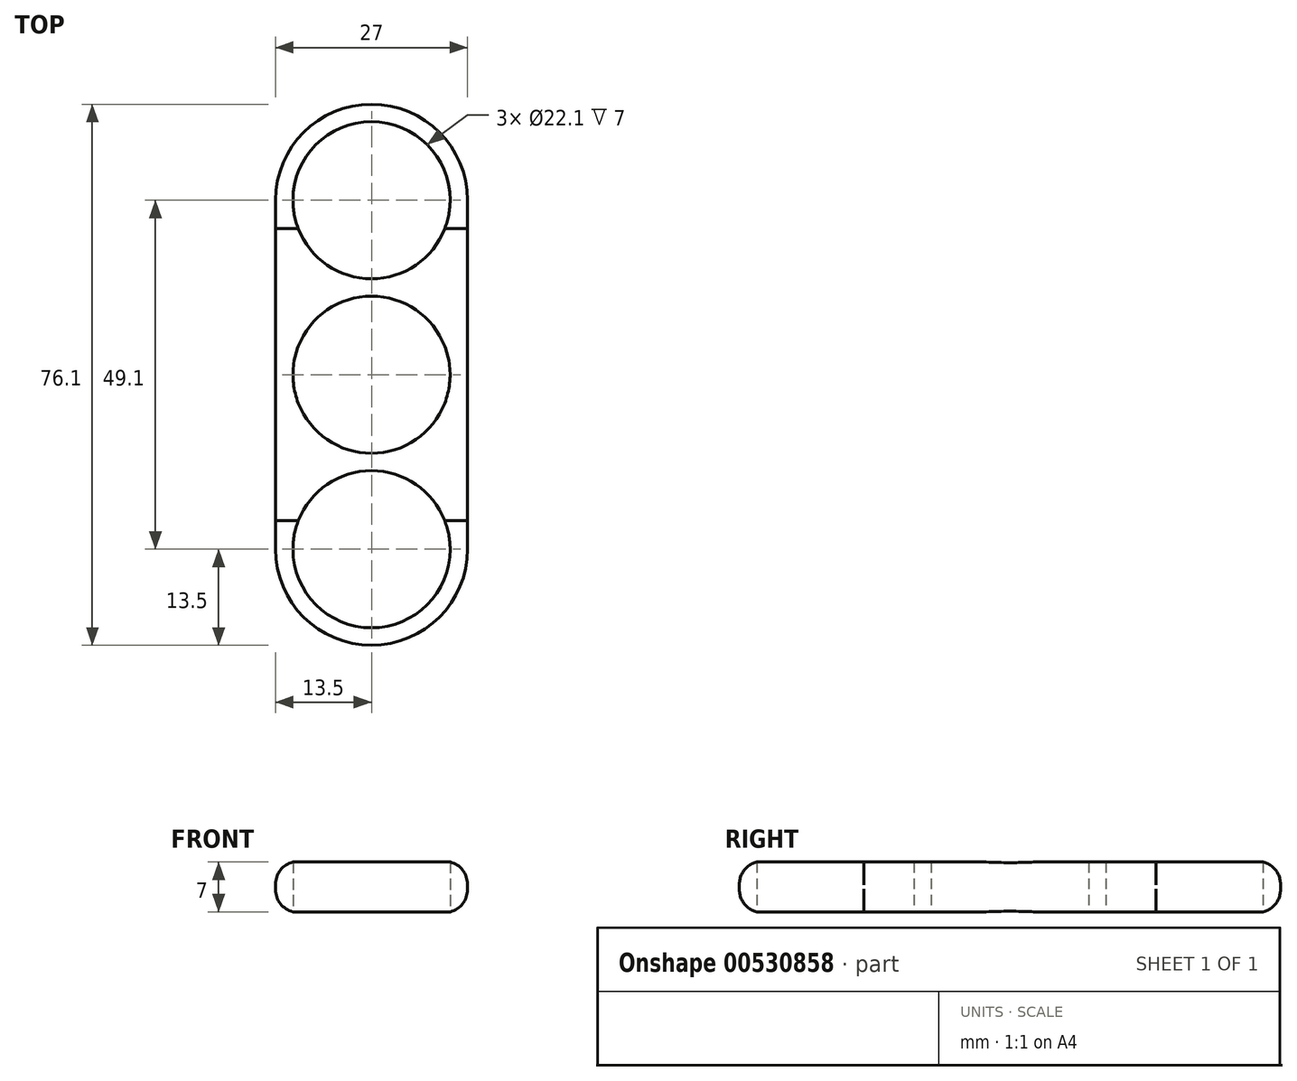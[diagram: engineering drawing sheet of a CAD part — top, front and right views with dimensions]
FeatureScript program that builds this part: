
annotation { "Feature Type Name" : "Feature", "Feature Type Description" : "" }
export const myFeature = defineFeature(function(context is Context, id is Id, definition is map)
    precondition{}
    {
        {
            var Q0;
            Q0=qCreatedBy(makeId("Top.planeOp"),FACE);
            var sketch = newSketch(context, id + "F0", { "sketchPlane" : qUnion([Q0])});
            skCircle(sketch, "E0", {"center": v(0, 0) * mm, "radius": 11.05 * mm});
            skCircle(sketch, "E1", {"center": v(0, 24.55) * mm, "radius": 11.05 * mm});
            skArc(sketch, "E2", {"start": v(13.5, 24.55) * mm, "mid": v(0, 38.05) * mm, "end": v(-13.5, 24.55) * mm});
            skCircle(sketch, "E3", {"center": v(0, -24.55) * mm, "radius": 11.05 * mm});
            skArc(sketch, "E4", {"start": v(-13.5, -24.55) * mm, "mid": v(0, -38.05) * mm, "end": v(13.5, -24.55) * mm});
            skLineSegment(sketch, "E5", {"start": v(13.5, -24.55) * mm, "end": v(13.5, 24.55) * mm});
            skLineSegment(sketch, "E6", {"start": v(-13.5, 24.55) * mm, "end": v(-13.5, -24.55) * mm});
            skSolve(sketch);
        }
        {
            var Q0;
            Q0=makeQuery(id+"F0.imprint","IMPRINT",FACE,{"disambiguationData":[TD([[makeQuery(id+"F0.imprint","IMPRINT",EDGE,{"derivedFrom":sQuery(id+"F0.wireOp",EDGE,"E0")}),-1.0]])]});
            extrude(context, id + "F1", {"entities" : qUnion([Q0]), "depth" : 7 * mm, "offsetDistance" : 25.4 * mm});
        }
        {
            var Q0;
            Q0=makeQuery(id+"F1.opExtrude","CAP_EDGE",EDGE,{"disambiguationData":[OSD([sQuery(id+"F0.wireOp",EDGE,"E5")])],"isStart":false});
            var Q1;
            Q1=makeQuery(id+"F1.opExtrude","CAP_EDGE",EDGE,{"disambiguationData":[OSD([sQuery(id+"F0.wireOp",EDGE,"E5")])],"isStart":true});
            var Q2;
            Q2=makeQuery(id+"F1.opExtrude","CAP_EDGE",EDGE,{"disambiguationData":[OSD([sQuery(id+"F0.wireOp",EDGE,"E6")])],"isStart":false});
            var Q3;
            Q3=makeQuery(id+"F1.opExtrude","CAP_EDGE",EDGE,{"disambiguationData":[OSD([sQuery(id+"F0.wireOp",EDGE,"E6")])],"isStart":true});
            var Q4;
            Q4=makeQuery(id+"F1.opExtrude","CAP_EDGE",EDGE,{"disambiguationData":[OSD([sQuery(id+"F0.wireOp",EDGE,"E4")])],"isStart":true});
            var Q5;
            Q5=makeQuery(id+"F1.opExtrude","SWEPT_FACE",FACE,{"disambiguationData":[OSD([sQuery(id+"F0.wireOp",EDGE,"E4")])]});
            var Q6;
            Q6=makeQuery(id+"F1.opExtrude","CAP_EDGE",EDGE,{"disambiguationData":[OSD([sQuery(id+"F0.wireOp",EDGE,"E2")])],"isStart":false});
            var Q7;
            Q7=makeQuery(id+"F1.opExtrude","CAP_EDGE",EDGE,{"disambiguationData":[OSD([sQuery(id+"F0.wireOp",EDGE,"E2")])],"isStart":true});
            fillet(context, id + "F2", {"entities" : qUnion([Q0, Q1, Q2, Q3, Q4, Q5, Q6, Q7]), "radius" : 3.2 * mm, "tangentPropagation" : true, "allowEdgeOverflow" : false});
        }
    });
